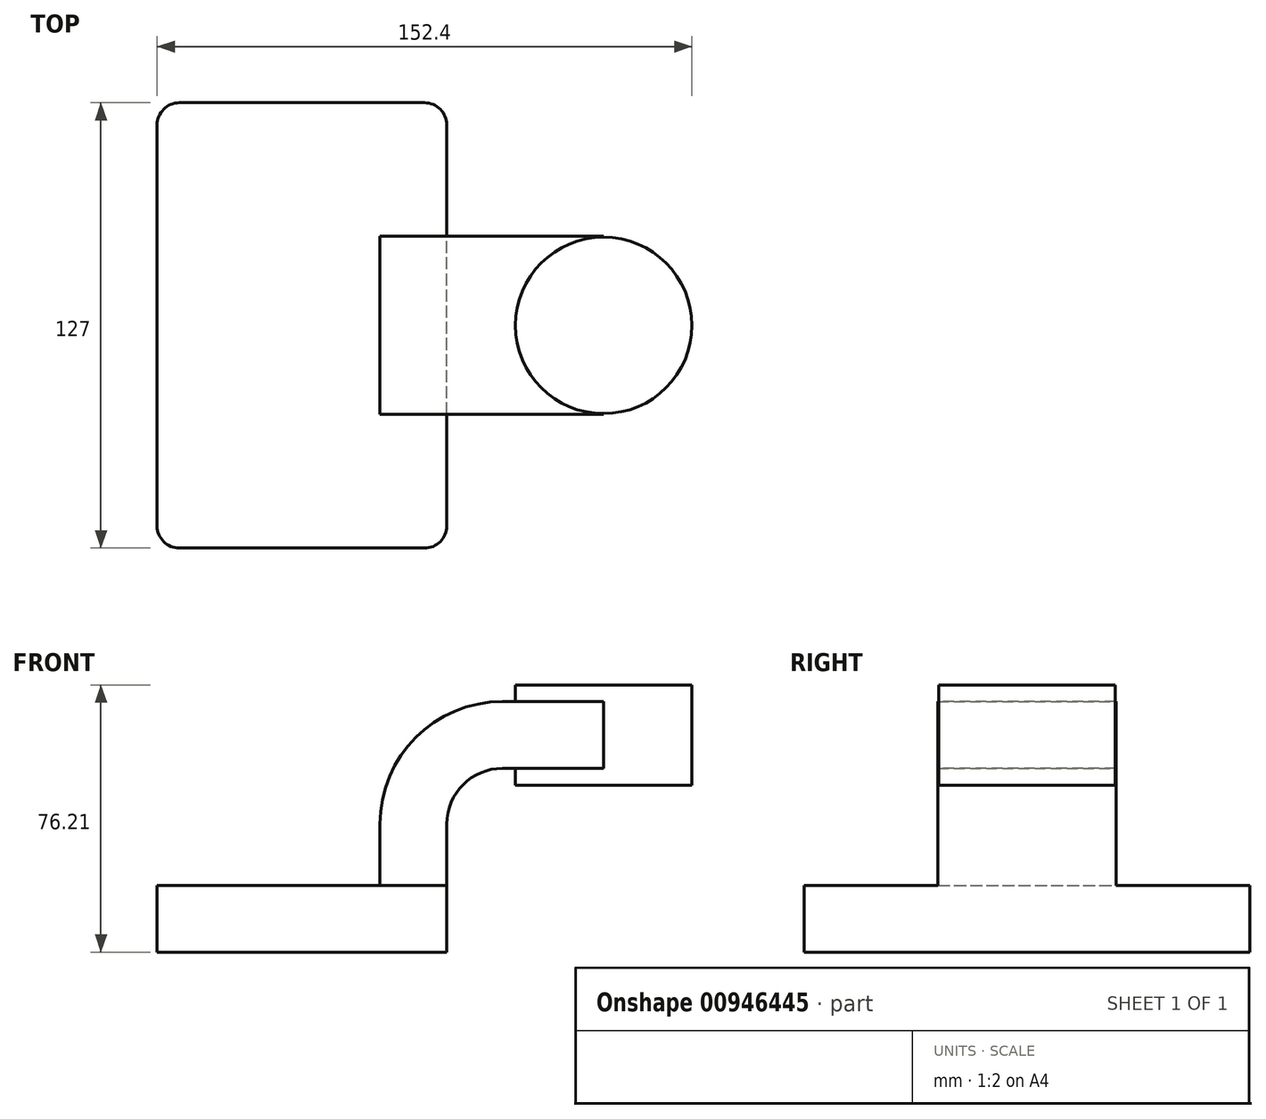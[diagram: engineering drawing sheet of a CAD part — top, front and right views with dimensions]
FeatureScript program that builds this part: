
annotation { "Feature Type Name" : "Feature", "Feature Type Description" : "" }
export const myFeature = defineFeature(function(context is Context, id is Id, definition is map)
    precondition{}
    {
        {
            var Q0;
            Q0=qCreatedBy(makeId("Front.planeOp"),FACE);
            var sketch = newSketch(context, id + "F0", { "sketchPlane" : qUnion([Q0])});
            skLineSegment(sketch, "E0.bottom", {"start": v(-41.28, 9.52) * mm, "end": v(41.27, 9.53) * mm});
            skLineSegment(sketch, "E0.top", {"start": v(-41.28, -9.53) * mm, "end": v(41.28, -9.53) * mm});
            skLineSegment(sketch, "E0.left", {"start": v(-41.28, 9.52) * mm, "end": v(-41.28, -9.53) * mm});
            skLineSegment(sketch, "E0.right", {"start": v(41.27, 9.53) * mm, "end": v(41.28, -9.52) * mm});
            skPoint(sketch, "E0.middle", {"position": v(0, 0) * mm});
            skLineSegment(sketch, "E1.bottom", {"start": v(60.32, 66.67) * mm, "end": v(111.12, 66.67) * mm});
            skLineSegment(sketch, "E1.top", {"start": v(60.33, 38.1) * mm, "end": v(111.12, 38.1) * mm});
            skLineSegment(sketch, "E1.left", {"start": v(60.32, 66.68) * mm, "end": v(60.33, 38.1) * mm});
            skLineSegment(sketch, "E1.right", {"start": v(111.12, 66.68) * mm, "end": v(111.12, 38.1) * mm});
            skPoint(sketch, "E1.middle", {"position": v(85.72, 52.39) * mm});
            skLineSegment(sketch, "E2", {"start": v(41.27, 9.53) * mm, "end": v(41.27, 27) * mm});
            skArc(sketch, "E3", {"start": v(41.27, 27) * mm, "mid": v(45.92, 38.23) * mm, "end": v(57.15, 42.88) * mm});
            skLineSegment(sketch, "E4", {"start": v(57.15, 42.88) * mm, "end": v(85.98, 42.88) * mm});
            skLineSegment(sketch, "E5.0", {"start": v(57.15, 61.93) * mm, "end": v(85.98, 61.93) * mm});
            skArc(sketch, "E5.1", {"start": v(22.22, 27) * mm, "mid": v(32.45, 51.7) * mm, "end": v(57.15, 61.93) * mm});
            skLineSegment(sketch, "E5.2", {"start": v(22.22, 9.53) * mm, "end": v(22.22, 27) * mm});
            skLineSegment(sketch, "E6", {"start": v(85.98, 61.93) * mm, "end": v(85.98, 42.88) * mm});
            skLineSegment(sketch, "E7", {"start": v(85.98, 61.93) * mm, "end": v(85.98, 66.67) * mm});
            skLineSegment(sketch, "E8", {"start": v(85.98, 66.67) * mm, "end": v(85.98, 42.88) * mm});
            skLineSegment(sketch, "E9", {"start": v(85.98, 42.88) * mm, "end": v(85.98, 38.1) * mm});
            skPoint(sketch, "E9.endSnap0", {"position": v(85.72, 38.1) * mm});
            skFitSpline(sketch, "E10", {"points": [v(-41.28, 9.52) * mm, v(57.15, 61.93) * mm], "startDerivative": vector(0.27, 60.25) * mm, "endDerivative": vector(171.45, -15.8) * mm});
            skSolve(sketch);
        }
        {
            var Q0;
            Q0=makeQuery(id+"F0.imprint","IMPRINT",FACE,{"disambiguationData":[TD([[makeQuery(id+"F0.imprint","IMPRINT",EDGE,{"derivedFrom":sQuery(id+"F0.wireOp",EDGE,"E0.top")}),1.0]])]});
            extrude(context, id + "F1", {"entities" : qUnion([Q0]), "endBound" : BoundingType.SYMMETRIC, "depth" : 127 * mm, "offsetDistance" : 25.4 * mm});
        }
        {
            var Q0;
            {var subQ0=sQuery(id+"F0.wireOp",EDGE,"E5.0");var subQ1=sQuery(id+"F0.wireOp",EDGE,"E1.left");var subQ2=makeQuery(id+"F0.imprint","INTERSECT",VERTEX,{"derivedFrom":[subQ1,subQ0]});Q0=makeQuery(id+"F0.imprint","IMPRINT",FACE,{"disambiguationData":[TD([[makeQuery(id+"F0.imprint","IMPRINT",EDGE,{"disambiguationData":[TD([[subQ2,-1.0]])],"derivedFrom":subQ1}),1.0]])]});}
            var Q1;
            {var subQ1=sQuery(id+"F0.wireOp",EDGE,"E2");Q1=makeQuery(id+"F0.imprint","IMPRINT",FACE,{"disambiguationData":[TD([[makeQuery(id+"F0.imprint","IMPRINT",EDGE,{"derivedFrom":subQ1}),1.0]])]});}
            extrude(context, id + "F2", {"entities" : qUnion([Q0, Q1]), "operationType" : NewBodyOperationType.ADD, "endBound" : BoundingType.SYMMETRIC, "depth" : 50.8 * mm, "offsetDistance" : 25.4 * mm});
        }
        {
            var Q0;
            Q0=makeQuery(id+"F0.imprint","IMPRINT",FACE,{"disambiguationData":[TD([[makeQuery(id+"F0.imprint","IMPRINT",EDGE,{"derivedFrom":sQuery(id+"F0.wireOp",EDGE,"E5.1")}),1.0]])]});
            extrude(context, id + "F3", {"entities" : qUnion([Q0]), "operationType" : NewBodyOperationType.ADD, "endBound" : BoundingType.SYMMETRIC, "depth" : 15.88 * mm, "offsetDistance" : 25.4 * mm});
        }
        {
            var Q0;
            {var subQ0=sQuery(id+"F0.wireOp",EDGE,"E1.right");Q0=makeQuery(id+"F0.imprint","IMPRINT",FACE,{"disambiguationData":[TD([[makeQuery(id+"F0.imprint","IMPRINT",EDGE,{"derivedFrom":subQ0}),-1.0]])]});}
            var Q1;
            Q1=sQuery(id+"F0.wireOp",EDGE,"E8");
            revolve(context, id + "F4", {"operationType" : NewBodyOperationType.ADD, "surfaceOperationType" : NewSurfaceOperationType.NEW, "entities" : qUnion([Q0]), "axis" : qUnion([Q1]), "revolveType" : RevolveType.FULL});
        }
        {
            var Q0;
            Q0=makeQuery(id+"F1.opExtrude","CAP_EDGE",EDGE,{"disambiguationData":[OSD([sQuery(id+"F0.wireOp",EDGE,"E0.right")])],"isStart":false});
            var Q1;
            Q1=makeQuery(id+"F1.opExtrude","CAP_EDGE",EDGE,{"disambiguationData":[OSD([sQuery(id+"F0.wireOp",EDGE,"E0.left")])],"isStart":false});
            var Q2;
            Q2=makeQuery(id+"F1.opExtrude","CAP_EDGE",EDGE,{"disambiguationData":[OSD([sQuery(id+"F0.wireOp",EDGE,"E0.right")])],"isStart":true});
            var Q3;
            Q3=makeQuery(id+"F1.opExtrude","CAP_EDGE",EDGE,{"disambiguationData":[OSD([sQuery(id+"F0.wireOp",EDGE,"E0.left")])],"isStart":true});
            fillet(context, id + "F5", {"entities" : qUnion([Q0, Q1, Q2, Q3]), "radius" : 6.35 * mm, "tangentPropagation" : true, "allowEdgeOverflow" : false});
        }
    });
